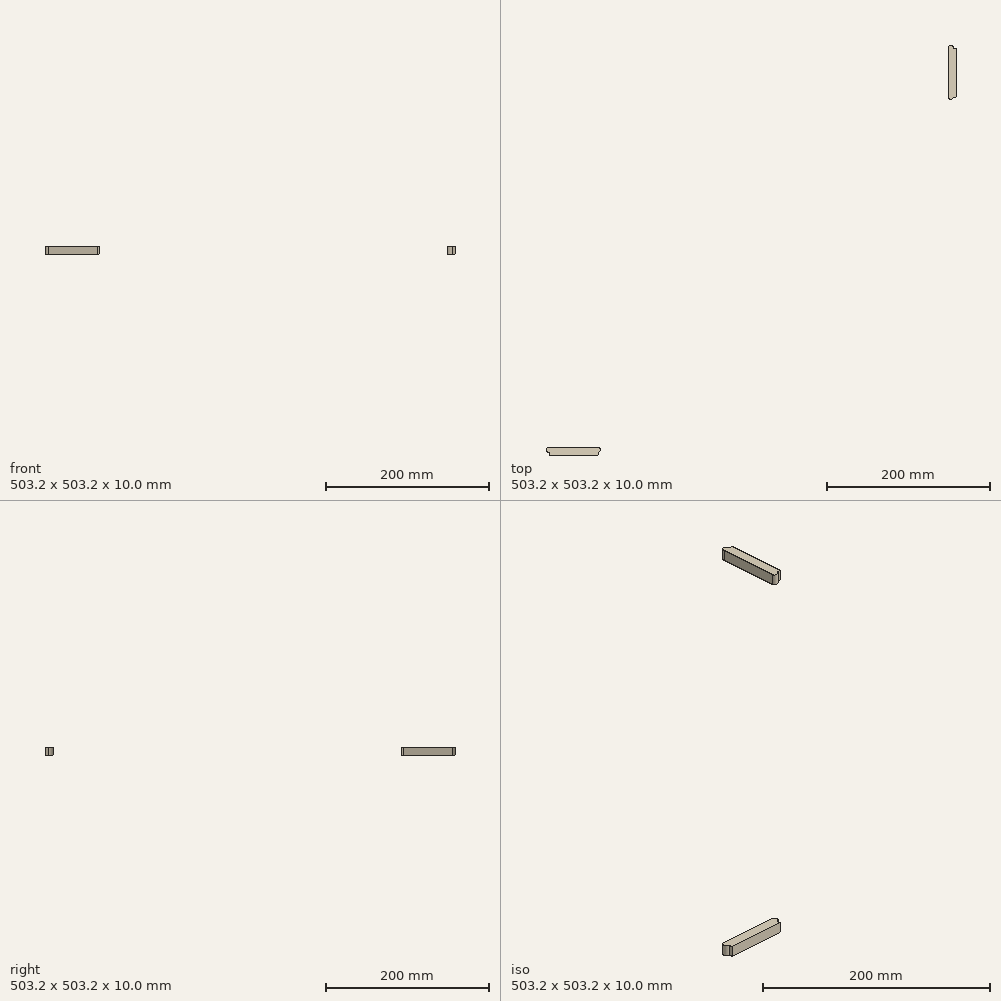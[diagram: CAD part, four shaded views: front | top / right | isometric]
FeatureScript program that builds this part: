
annotation { "Feature Type Name" : "Feature", "Feature Type Description" : "" }
export const myFeature = defineFeature(function(context is Context, id is Id, definition is map)
    precondition{}
    {
        {
            var Q0;
            Q0=qCreatedBy(makeId("Top.planeOp"),FACE);
            var sketch = newSketch(context, id + "F0", { "sketchPlane" : qUnion([Q0])});
            skLineSegment(sketch, "E0.bottom", {"start": v(290, -290) * mm, "end": v(-290, -290) * mm});
            skLineSegment(sketch, "E0.top", {"start": v(290, 290) * mm, "end": v(-290, 290) * mm});
            skLineSegment(sketch, "E0.left", {"start": v(290, -290) * mm, "end": v(290, 290) * mm});
            skLineSegment(sketch, "E0.right", {"start": v(-290, -290) * mm, "end": v(-290, 290) * mm});
            skPoint(sketch, "E0.middle", {"position": v(0, 0) * mm});
            skSolve(sketch);
        }
        {
            var Q0;
            Q0=makeQuery(id+"F0.imprint","IMPRINT",FACE,{"disambiguationData":[TD([[makeQuery(id+"F0.imprint","IMPRINT",EDGE,{"derivedFrom":sQuery(id+"F0.wireOp",EDGE,"E0.bottom")}),-1.0]])]});
            extrude(context, id + "F1", {"entities" : qUnion([Q0]), "depth" : 10 * mm, "offsetDistance" : 25 * mm});
        }
        {
            var Q0;
            Q0=makeQuery(id+"F1.opExtrude","CAP_FACE",FACE,{"disambiguationData":[OSD([sQuery(id+"F0.wireOp",EDGE,"E0.bottom"),sQuery(id+"F0.wireOp",EDGE,"E0.top"),sQuery(id+"F0.wireOp",EDGE,"E0.left"),sQuery(id+"F0.wireOp",EDGE,"E0.right")])],"isStart":false});
            var sketch = newSketch(context, id + "F2", { "sketchPlane" : qUnion([Q0])});
            skLineSegment(sketch, "E1", {"start": v(0, 280) * mm, "end": v(-55, 280) * mm});
            skPoint(sketch, "E1.startSnap0", {"position": v(0, 290) * mm});
            skLineSegment(sketch, "E2", {"start": v(-55, 290) * mm, "end": v(-150, 290) * mm});
            skLineSegment(sketch, "E3", {"start": v(-150, 290) * mm, "end": v(-150, 286.5) * mm});
            skLineSegment(sketch, "E4", {"start": v(-150, 280) * mm, "end": v(-210, 280) * mm});
            skLineSegment(sketch, "E5", {"start": v(-210, 286.5) * mm, "end": v(-210, 290) * mm});
            skLineSegment(sketch, "E6", {"start": v(-210, 290) * mm, "end": v(-290, 290) * mm});
            skLineSegment(sketch, "E7", {"start": v(-290, 290) * mm, "end": v(-290, 210) * mm});
            skLineSegment(sketch, "E8", {"start": v(-290, 210) * mm, "end": v(-286.5, 210) * mm});
            skLineSegment(sketch, "E9", {"start": v(-280, 210) * mm, "end": v(-280, 150) * mm});
            skLineSegment(sketch, "E10", {"start": v(-290, 150) * mm, "end": v(-290, 55) * mm});
            skLineSegment(sketch, "E11", {"start": v(-290, 55) * mm, "end": v(-286.5, 55) * mm});
            skLineSegment(sketch, "E12", {"start": v(-280, 55) * mm, "end": v(-280, 0) * mm});
            skPoint(sketch, "E13.MirrorP", {"position": v(0, 275) * mm});
            skArc(sketch, "E14", {"start": v(-55, 286.5) * mm, "mid": v(-58.25, 283.25) * mm, "end": v(-55, 280) * mm});
            skLineSegment(sketch, "E15.trimOffspring", {"start": v(-55, 286.5) * mm, "end": v(-55, 290) * mm});
            skArc(sketch, "E16", {"start": v(-150, 280) * mm, "mid": v(-146.75, 283.25) * mm, "end": v(-150, 286.5) * mm});
            skArc(sketch, "E17", {"start": v(-210, 286.5) * mm, "mid": v(-213.25, 283.25) * mm, "end": v(-210, 280) * mm});
            skArc(sketch, "E18", {"start": v(-280, 210) * mm, "mid": v(-283.25, 213.25) * mm, "end": v(-286.5, 210) * mm});
            skArc(sketch, "E19", {"start": v(-286.5, 150) * mm, "mid": v(-283.25, 146.75) * mm, "end": v(-280, 150) * mm});
            skLineSegment(sketch, "E20.trimOffspring", {"start": v(-286.5, 150) * mm, "end": v(-290, 150) * mm});
            skArc(sketch, "E21", {"start": v(-280, 55) * mm, "mid": v(-283.25, 58.25) * mm, "end": v(-286.5, 55) * mm});
            skLineSegment(sketch, "E22", {"start": v(0, 339) * mm, "end": v(0, -413.46) * mm, "construction": true});
            skLineSegment(sketch, "E23", {"start": v(387.23, 0) * mm, "end": v(-415.93, 0) * mm, "construction": true});
            skArc(sketch, "E24.MirrorCS", {"start": v(286.5, 150) * mm, "mid": v(283.25, 146.75) * mm, "end": v(280, 150) * mm});
            skLineSegment(sketch, "E25.MirrorCS", {"start": v(286.5, 150) * mm, "end": v(290, 150) * mm});
            skArc(sketch, "E26.MirrorCS", {"start": v(55, 286.5) * mm, "mid": v(58.25, 283.25) * mm, "end": v(55, 280) * mm});
            skLineSegment(sketch, "E27.MirrorCS", {"start": v(210, 286.5) * mm, "end": v(210, 290) * mm});
            skLineSegment(sketch, "E28.MirrorCS", {"start": v(55, 286.5) * mm, "end": v(55, 290) * mm});
            skLineSegment(sketch, "E29.MirrorCS", {"start": v(150, 290) * mm, "end": v(150, 286.5) * mm});
            skArc(sketch, "E30.MirrorCS", {"start": v(210, 286.5) * mm, "mid": v(213.25, 283.25) * mm, "end": v(210, 280) * mm});
            skArc(sketch, "E31.MirrorCS", {"start": v(150, 280) * mm, "mid": v(146.75, 283.25) * mm, "end": v(150, 286.5) * mm});
            skLineSegment(sketch, "E32.MirrorCS", {"start": v(290, 210) * mm, "end": v(286.5, 210) * mm});
            skLineSegment(sketch, "E33.MirrorCS", {"start": v(290, 55) * mm, "end": v(286.5, 55) * mm});
            skArc(sketch, "E34.MirrorCS", {"start": v(280, 210) * mm, "mid": v(283.25, 213.25) * mm, "end": v(286.5, 210) * mm});
            skArc(sketch, "E35.MirrorCS", {"start": v(280, 55) * mm, "mid": v(283.25, 58.25) * mm, "end": v(286.5, 55) * mm});
            skLineSegment(sketch, "E36.MirrorCS", {"start": v(280, 210) * mm, "end": v(280, 150) * mm});
            skLineSegment(sketch, "E37.MirrorCS", {"start": v(0, 280) * mm, "end": v(55, 280) * mm});
            skLineSegment(sketch, "E38.MirrorCS", {"start": v(55, 290) * mm, "end": v(150, 290) * mm});
            skLineSegment(sketch, "E39.MirrorCS", {"start": v(150, 280) * mm, "end": v(210, 280) * mm});
            skLineSegment(sketch, "E40.MirrorCS", {"start": v(290, 150) * mm, "end": v(290, 55) * mm});
            skLineSegment(sketch, "E41.MirrorCS", {"start": v(280, 55) * mm, "end": v(280, 0) * mm});
            skLineSegment(sketch, "E42.MirrorCS", {"start": v(210, 290) * mm, "end": v(290, 290) * mm});
            skLineSegment(sketch, "E43.MirrorCS", {"start": v(290, 290) * mm, "end": v(290, 210) * mm});
            skPoint(sketch, "E44.MirrorP", {"position": v(0, -275) * mm});
            skArc(sketch, "E45.MirrorCS", {"start": v(-210, -286.5) * mm, "mid": v(-213.25, -283.25) * mm, "end": v(-210, -280) * mm});
            skLineSegment(sketch, "E46.MirrorCS", {"start": v(-150, -290) * mm, "end": v(-150, -286.5) * mm});
            skLineSegment(sketch, "E47.MirrorCS", {"start": v(-210, -286.5) * mm, "end": v(-210, -290) * mm});
            skArc(sketch, "E48.MirrorCS", {"start": v(-150, -280) * mm, "mid": v(-146.75, -283.25) * mm, "end": v(-150, -286.5) * mm});
            skLineSegment(sketch, "E49.MirrorCS", {"start": v(-55, -286.5) * mm, "end": v(-55, -290) * mm});
            skArc(sketch, "E50.MirrorCS", {"start": v(-55, -286.5) * mm, "mid": v(-58.25, -283.25) * mm, "end": v(-55, -280) * mm});
            skArc(sketch, "E51.MirrorCS", {"start": v(280, -55) * mm, "mid": v(283.25, -58.25) * mm, "end": v(286.5, -55) * mm});
            skLineSegment(sketch, "E52.MirrorCS", {"start": v(290, -55) * mm, "end": v(286.5, -55) * mm});
            skArc(sketch, "E53.MirrorCS", {"start": v(280, -210) * mm, "mid": v(283.25, -213.25) * mm, "end": v(286.5, -210) * mm});
            skArc(sketch, "E54.MirrorCS", {"start": v(55, -286.5) * mm, "mid": v(58.25, -283.25) * mm, "end": v(55, -280) * mm});
            skArc(sketch, "E55.MirrorCS", {"start": v(210, -286.5) * mm, "mid": v(213.25, -283.25) * mm, "end": v(210, -280) * mm});
            skLineSegment(sketch, "E56.MirrorCS", {"start": v(-286.5, -150) * mm, "end": v(-290, -150) * mm});
            skLineSegment(sketch, "E57.MirrorCS", {"start": v(210, -286.5) * mm, "end": v(210, -290) * mm});
            skLineSegment(sketch, "E58.MirrorCS", {"start": v(-290, -210) * mm, "end": v(-286.5, -210) * mm});
            skLineSegment(sketch, "E59.MirrorCS", {"start": v(55, -286.5) * mm, "end": v(55, -290) * mm});
            skArc(sketch, "E60.MirrorCS", {"start": v(150, -280) * mm, "mid": v(146.75, -283.25) * mm, "end": v(150, -286.5) * mm});
            skArc(sketch, "E61.MirrorCS", {"start": v(-286.5, -150) * mm, "mid": v(-283.25, -146.75) * mm, "end": v(-280, -150) * mm});
            skLineSegment(sketch, "E62.MirrorCS", {"start": v(150, -290) * mm, "end": v(150, -286.5) * mm});
            skLineSegment(sketch, "E63.MirrorCS", {"start": v(290, -210) * mm, "end": v(286.5, -210) * mm});
            skArc(sketch, "E64.MirrorCS", {"start": v(-280, -55) * mm, "mid": v(-283.25, -58.25) * mm, "end": v(-286.5, -55) * mm});
            skLineSegment(sketch, "E65.MirrorCS", {"start": v(-290, -55) * mm, "end": v(-286.5, -55) * mm});
            skArc(sketch, "E66.MirrorCS", {"start": v(-280, -210) * mm, "mid": v(-283.25, -213.25) * mm, "end": v(-286.5, -210) * mm});
            skArc(sketch, "E67.MirrorCS", {"start": v(286.5, -150) * mm, "mid": v(283.25, -146.75) * mm, "end": v(280, -150) * mm});
            skLineSegment(sketch, "E68.MirrorCS", {"start": v(286.5, -150) * mm, "end": v(290, -150) * mm});
            skPoint(sketch, "E69.MirrorP", {"position": v(0, -290) * mm});
            skLineSegment(sketch, "E70.MirrorCS", {"start": v(0, -280) * mm, "end": v(55, -280) * mm});
            skLineSegment(sketch, "E71.MirrorCS", {"start": v(55, -290) * mm, "end": v(150, -290) * mm});
            skLineSegment(sketch, "E72.MirrorCS", {"start": v(-280, -210) * mm, "end": v(-280, -150) * mm});
            skLineSegment(sketch, "E73.MirrorCS", {"start": v(280, -210) * mm, "end": v(280, -150) * mm});
            skLineSegment(sketch, "E74.MirrorCS", {"start": v(-55, -290) * mm, "end": v(-150, -290) * mm});
            skLineSegment(sketch, "E75.MirrorCS", {"start": v(-280, -55) * mm, "end": v(-280, 0) * mm});
            skLineSegment(sketch, "E76.MirrorCS", {"start": v(-290, -290) * mm, "end": v(-290, -210) * mm});
            skLineSegment(sketch, "E77.MirrorCS", {"start": v(290, -150) * mm, "end": v(290, -55) * mm});
            skLineSegment(sketch, "E78.MirrorCS", {"start": v(210, -290) * mm, "end": v(290, -290) * mm});
            skLineSegment(sketch, "E79.MirrorCS", {"start": v(-290, -150) * mm, "end": v(-290, -55) * mm});
            skLineSegment(sketch, "E80.MirrorCS", {"start": v(150, -280) * mm, "end": v(210, -280) * mm});
            skLineSegment(sketch, "E81.MirrorCS", {"start": v(280, -55) * mm, "end": v(280, 0) * mm});
            skLineSegment(sketch, "E82.MirrorCS", {"start": v(290, -290) * mm, "end": v(290, -210) * mm});
            skLineSegment(sketch, "E83.MirrorCS", {"start": v(-210, -290) * mm, "end": v(-290, -290) * mm});
            skLineSegment(sketch, "E84.MirrorCS", {"start": v(-150, -280) * mm, "end": v(-210, -280) * mm});
            skLineSegment(sketch, "E85.MirrorCS", {"start": v(0, -280) * mm, "end": v(-55, -280) * mm});
            skSolve(sketch);
        }
        {
            var Q0;
            {var subQ1=sQuery(id+"F2.wireOp",EDGE,"E3");Q0=makeQuery(id+"F2.imprint","IMPRINT",FACE,{"disambiguationData":[TD([[makeQuery(id+"F2.imprint","IMPRINT",EDGE,{"derivedFrom":subQ1}),-1.0]])]});}
            var Q1;
            Q1=makeQuery(id+"F2.imprint","IMPRINT",FACE,{"disambiguationData":[TD([[makeQuery(id+"F2.imprint","IMPRINT",EDGE,{"derivedFrom":sQuery(id+"F2.wireOp",EDGE,"E1")}),-1.0]])]});
            var Q2;
            {var subQ1=sQuery(id+"F2.wireOp",EDGE,"E27.MirrorCS");Q2=makeQuery(id+"F2.imprint","IMPRINT",FACE,{"disambiguationData":[TD([[makeQuery(id+"F2.imprint","IMPRINT",EDGE,{"derivedFrom":subQ1}),1.0]])]});}
            var Q3;
            Q3=makeQuery(id+"F2.imprint","IMPRINT",FACE,{"disambiguationData":[TD([[makeQuery(id+"F2.imprint","IMPRINT",EDGE,{"derivedFrom":sQuery(id+"F2.wireOp",EDGE,"E24.MirrorCS")}),-1.0]])]});
            var Q4;
            {var subQ0=sQuery(id+"F2.wireOp",EDGE,"E33.MirrorCS");Q4=makeQuery(id+"F2.imprint","IMPRINT",FACE,{"disambiguationData":[TD([[makeQuery(id+"F2.imprint","IMPRINT",EDGE,{"derivedFrom":subQ0}),1.0]])]});}
            var Q5;
            Q5=makeQuery(id+"F2.imprint","IMPRINT",FACE,{"disambiguationData":[TD([[makeQuery(id+"F2.imprint","IMPRINT",EDGE,{"derivedFrom":sQuery(id+"F2.wireOp",EDGE,"E53.MirrorCS")}),1.0]])]});
            var Q6;
            Q6=makeQuery(id+"F2.imprint","IMPRINT",FACE,{"disambiguationData":[TD([[makeQuery(id+"F2.imprint","IMPRINT",EDGE,{"derivedFrom":sQuery(id+"F2.wireOp",EDGE,"E55.MirrorCS")}),1.0]])]});
            var Q7;
            {var subQ1=sQuery(id+"F2.wireOp",EDGE,"E49.MirrorCS");Q7=makeQuery(id+"F2.imprint","IMPRINT",FACE,{"disambiguationData":[TD([[makeQuery(id+"F2.imprint","IMPRINT",EDGE,{"derivedFrom":subQ1}),1.0]])]});}
            var Q8;
            Q8=makeQuery(id+"F2.imprint","IMPRINT",FACE,{"disambiguationData":[TD([[makeQuery(id+"F2.imprint","IMPRINT",EDGE,{"derivedFrom":sQuery(id+"F2.wireOp",EDGE,"E45.MirrorCS")}),-1.0]])]});
            var Q9;
            {var subQ1=sQuery(id+"F2.wireOp",EDGE,"E56.MirrorCS");Q9=makeQuery(id+"F2.imprint","IMPRINT",FACE,{"disambiguationData":[TD([[makeQuery(id+"F2.imprint","IMPRINT",EDGE,{"derivedFrom":subQ1}),1.0]])]});}
            var Q10;
            {var subQ0=sQuery(id+"F2.wireOp",EDGE,"E11");Q10=makeQuery(id+"F2.imprint","IMPRINT",FACE,{"disambiguationData":[TD([[makeQuery(id+"F2.imprint","IMPRINT",EDGE,{"derivedFrom":subQ0}),-1.0]])]});}
            var Q11;
            {var subQ0=sQuery(id+"F2.wireOp",EDGE,"E8");Q11=makeQuery(id+"F2.imprint","IMPRINT",FACE,{"disambiguationData":[TD([[makeQuery(id+"F2.imprint","IMPRINT",EDGE,{"derivedFrom":subQ0}),-1.0]])]});}
            extrude(context, id + "F3", {"entities" : qUnion([Q0, Q1, Q2, Q3, Q4, Q5, Q6, Q7, Q8, Q9, Q10, Q11]), "operationType" : NewBodyOperationType.REMOVE, "endBound" : BoundingType.THROUGH_ALL, "oppositeDirection" : true, "depth" : 25 * mm, "offsetDistance" : 25 * mm});
        }
    });
